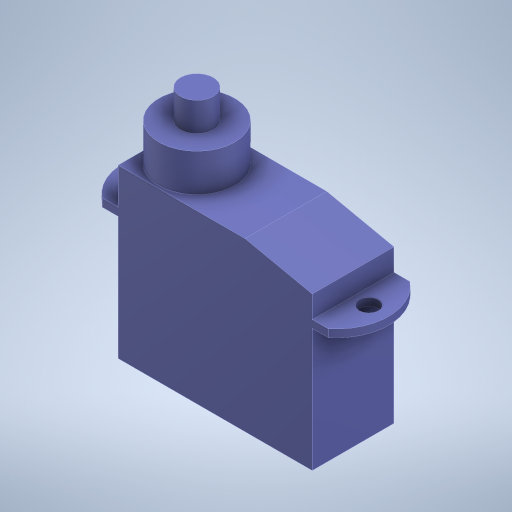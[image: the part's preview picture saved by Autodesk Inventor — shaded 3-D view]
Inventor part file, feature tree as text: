
AUTODESK INVENTOR PART (.ipt)
format: ipt  version: 2024 (Build 280153000, 153)  size: 280,576 bytes
history: native  units: in
note: dims shown in document units (in); Inventor stores cm internally (conversion verified against a paired STEP export)
features: chamfer x1
ambient origin geometry x8: Origin, YZ Plane, XZ Plane, XY Plane, X Axis, Y Axis, Z Axis, Center Point
bodies: Solid1 (feature_tree), Body1 (feature_tree)
feature tree (1):
  chamfer  "Chamfer1"  Distance=0.2756in Angle=45.0deg
